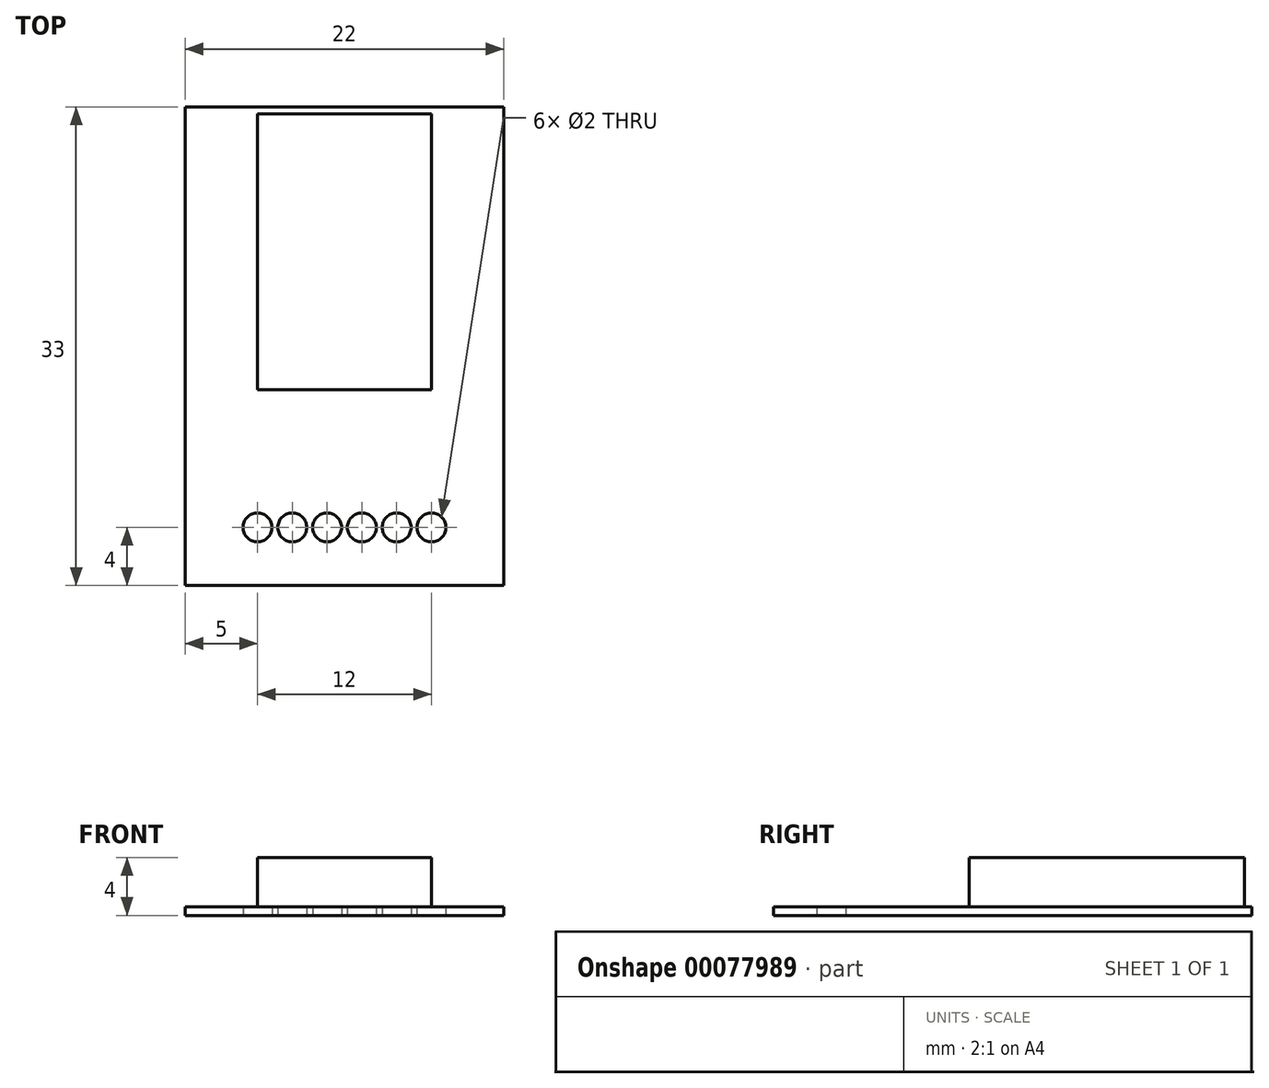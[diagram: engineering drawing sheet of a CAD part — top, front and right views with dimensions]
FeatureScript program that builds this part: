
annotation { "Feature Type Name" : "Feature", "Feature Type Description" : "" }
export const myFeature = defineFeature(function(context is Context, id is Id, definition is map)
    precondition{}
    {
        {
            var Q0;
            Q0=qCreatedBy(makeId("Top.planeOp"),FACE);
            var sketch = newSketch(context, id + "F0", { "sketchPlane" : qUnion([Q0])});
            skLineSegment(sketch, "E0", {"start": v(0, 0) * mm, "end": v(11, 0) * mm});
            skLineSegment(sketch, "E1", {"start": v(11, 0) * mm, "end": v(11, 33) * mm});
            skLineSegment(sketch, "E2", {"start": v(11, 33) * mm, "end": v(0, 33) * mm});
            skLineSegment(sketch, "E3", {"start": v(0, 3) * mm, "end": v(11, 3) * mm, "construction": true});
            skLineSegment(sketch, "E4", {"start": v(1, 5) * mm, "end": v(11, 5) * mm, "construction": true});
            skLineSegment(sketch, "E5", {"start": v(7, 5) * mm, "end": v(7, 3) * mm, "construction": true});
            skLineSegment(sketch, "E6.MirrorCS", {"start": v(-7, 5) * mm, "end": v(-7, 3) * mm, "construction": true});
            skLineSegment(sketch, "E7.MirrorCS", {"start": v(0, 3) * mm, "end": v(-11, 3) * mm, "construction": true});
            skLineSegment(sketch, "E8.MirrorCS", {"start": v(-1, 5) * mm, "end": v(-11, 5) * mm, "construction": true});
            skLineSegment(sketch, "E9.MirrorCS", {"start": v(0, 0) * mm, "end": v(-11, 0) * mm});
            skLineSegment(sketch, "E10.MirrorCS", {"start": v(-11, 0) * mm, "end": v(-11, 33) * mm});
            skLineSegment(sketch, "E11.MirrorCS", {"start": v(-11, 33) * mm, "end": v(0, 33) * mm});
            skCircle(sketch, "E12", {"center": v(6, 4) * mm, "radius": 1 * mm});
            skCircle(sketch, "E13.1.0.0", {"center": v(3.6, 4) * mm, "radius": 1 * mm});
            skCircle(sketch, "E13.2.0.0", {"center": v(1.2, 4) * mm, "radius": 1 * mm});
            skCircle(sketch, "E13.3.0.0", {"center": v(-1.2, 4) * mm, "radius": 1 * mm});
            skCircle(sketch, "E13.4.0.0", {"center": v(-3.6, 4) * mm, "radius": 1 * mm});
            skCircle(sketch, "E13.5.0.0", {"center": v(-6, 4) * mm, "radius": 1 * mm});
            skLineSegment(sketch, "E13.direction1", {"start": v(6, 4) * mm, "end": v(3.6, 4) * mm, "construction": true});
            skLineSegment(sketch, "E14.rect.bottom", {"start": v(-5.01, 3) * mm, "end": v(-6.99, 3) * mm, "construction": true});
            skLineSegment(sketch, "E14.rect.top", {"start": v(-5.01, 5) * mm, "end": v(-6.99, 5) * mm, "construction": true});
            skLineSegment(sketch, "E14.rect.left", {"start": v(-5.01, 3) * mm, "end": v(-5.01, 5) * mm, "construction": true});
            skLineSegment(sketch, "E14.rect.right", {"start": v(-6.99, 3) * mm, "end": v(-6.99, 5) * mm, "construction": true});
            skSolve(sketch);
        }
        {
            var Q0;
            Q0=qSketchRegion(id+"F0",true);
            extrude(context, id + "F1", {"entities" : qUnion([Q0]), "depth" : 0.6 * mm});
        }
        {
            var Q0;
            Q0=makeQuery(id+"F1.opExtrude","CAP_FACE",FACE,{"disambiguationData":[OSD([sQuery(id+"F0.wireOp",EDGE,"E0"),sQuery(id+"F0.wireOp",EDGE,"E1"),sQuery(id+"F0.wireOp",EDGE,"E2"),sQuery(id+"F0.wireOp",EDGE,"E9.MirrorCS"),sQuery(id+"F0.wireOp",EDGE,"E10.MirrorCS"),sQuery(id+"F0.wireOp",EDGE,"E11.MirrorCS"),sQuery(id+"F0.wireOp",EDGE,"E12"),sQuery(id+"F0.wireOp",EDGE,"E13.1.0.0"),sQuery(id+"F0.wireOp",EDGE,"E13.2.0.0"),sQuery(id+"F0.wireOp",EDGE,"E13.3.0.0"),sQuery(id+"F0.wireOp",EDGE,"E13.4.0.0"),sQuery(id+"F0.wireOp",EDGE,"E13.5.0.0")])],"isStart":false});
            var sketch = newSketch(context, id + "F2", { "sketchPlane" : qUnion([Q0])});
            skLineSegment(sketch, "E15", {"start": v(-6, 4) * mm, "end": v(-6, 32.5) * mm, "construction": true});
            skLineSegment(sketch, "E16", {"start": v(6, 4) * mm, "end": v(6, 32.5) * mm, "construction": true});
            skLineSegment(sketch, "E17", {"start": v(6, 13.5) * mm, "end": v(-6, 13.5) * mm});
            skLineSegment(sketch, "E18", {"start": v(-6, 13.5) * mm, "end": v(-6, 32.5) * mm});
            skLineSegment(sketch, "E19", {"start": v(6, 32.5) * mm, "end": v(6, 13.5) * mm});
            skLineSegment(sketch, "E20", {"start": v(-6, 32.5) * mm, "end": v(6, 32.5) * mm});
            skSolve(sketch);
        }
        {
            var Q0;
            Q0=qSketchRegion(id+"F2",true);
            extrude(context, id + "F3", {"entities" : qUnion([Q0]), "operationType" : NewBodyOperationType.ADD, "depth" : 3.4 * mm});
        }
    });
